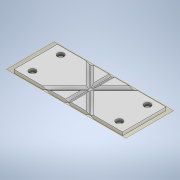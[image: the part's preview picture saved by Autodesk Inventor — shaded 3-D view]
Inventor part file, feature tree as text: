
AUTODESK INVENTOR PART (.ipt)
format: ipt  version: 2020 (Build 240168000, 168)  size: 274,944 bytes
history: native  units: mm
features: chamfer x24, projected_geometry x8, extrude x3, sketch x3, plane x1
ambient origin geometry x8: Origin, YZ Plane, XZ Plane, XY Plane, X Axis, Y Axis, Z Axis, Center Point
bodies: Solid1 (feature_tree)
feature tree (39):
  extrude  "Extrusion1"  Depth=20.0mm
  plane  "Work Plane1"
  extrude  "Extrusion2"  Depth=10.0mm
  chamfer  "Chamfer1"  Distance=10.0mm
  chamfer  "Chamfer2"  Distance=0.5mm
  chamfer  "Chamfer3"  Distance=25.0mm
  chamfer  "Chamfer4"  Distance=0.5mm
  chamfer  "Chamfer5"  Distance=50.0mm
  chamfer  "Chamfer6"  Distance=0.5mm
  chamfer  "Chamfer7"  Distance=50.0mm
  chamfer  "Chamfer8"  Distance=1.5mm
  chamfer  "Chamfer9"  Distance=0.29mm
  chamfer  "Chamfer10"  Distance=0.605mm Angle=60.0deg
  chamfer  "Chamfer11"  Distance=0.605mm Angle=60.0deg
  chamfer  "Chamfer12"  Distance=0.605mm Angle=60.0deg
  chamfer  "Chamfer13"  Distance=0.605mm Angle=60.0deg
  chamfer  "Chamfer14"  Distance=0.605mm Angle=60.0deg
  chamfer  "Chamfer15"  Distance=0.605mm Angle=60.0deg
  chamfer  "Chamfer16"  Distance=0.605mm Angle=60.0deg
  chamfer  "Chamfer17"  Distance=0.605mm Angle=60.0deg
  chamfer  "Chamfer18"  Distance=0.605mm Angle=60.0deg
  chamfer  "Chamfer19"  Distance=0.605mm Angle=60.0deg
  chamfer  "Chamfer20"  Distance=0.605mm Angle=60.0deg
  chamfer  "Chamfer21"  Distance=0.605mm Angle=60.0deg
  chamfer  "Chamfer22"  Distance=0.605mm Angle=60.0deg
  chamfer  "Chamfer23"  Distance=0.605mm Angle=60.0deg
  chamfer  "Chamfer24"  Distance=0.605mm Angle=60.0deg
  extrude  "Extrusion3"  Depth=0.605mm TaperAngle=60.0deg
  sketch  "Sketch1"  dims[d0=50.0mm d1=20.0mm]
  sketch  "Sketch2"  dims[d2=10.0mm d3=10.0mm]
  projected_geometry  "Projected Loop1"
  projected_geometry  "Projected Loop2"
  projected_geometry  "Projected Loop3"
  projected_geometry  "Projected Loop4"
  projected_geometry  "Projected Loop5"
  projected_geometry  "Projected Loop6"
  sketch  "Sketch3"  dims[d4=10.0mm d5=10.0mm d6=0.5mm d7=25.0mm d8=0.5mm d9=50.0mm d10=0.5mm d11=50.0mm d12=1.5mm d13=0.0mm d14=0.29mm d15=0.0mm d16=1.0mm d17=0.605mm d18=60.0deg d19=1.0mm d20=0.605mm d21=60.0deg d22=1.0mm d23=0.605mm d24=60.0deg d25=1.0mm d26=0.605mm d27=60.0deg d28=1.0mm d29=0.605mm d30=60.0deg d31=1.0mm d32=0.605mm d33=60.0deg d34=1.0mm d35=0.605mm d36=60.0deg d37=1.0mm d38=0.605mm d39=60.0deg d40=1.0mm d41=0.605mm d42=60.0deg d43=1.0mm d44=0.605mm d45=60.0deg d46=1.0mm d47=0.605mm d48=60.0deg d49=1.0mm d50=0.605mm d51=60.0deg d52=0.605mm d53=1.0mm d54=60.0deg d55=0.605mm d56=1.0mm d57=60.0deg d58=0.605mm d59=1.0mm d60=60.0deg d61=0.605mm d62=1.0mm d63=60.0deg d64=0.605mm d65=1.0mm d66=60.0deg d67=0.605mm d68=1.0mm d69=60.0deg d70=0.605mm d71=1.0mm d72=60.0deg d73=0.605mm d74=1.0mm d75=60.0deg d76=0.605mm d77=1.0mm d78=60.0deg d79=0.605mm d80=1.0mm d81=60.0deg d82=0.605mm d83=1.0mm d84=60.0deg d85=0.605mm d86=1.0mm d87=60.0deg d88=13.0mm d89=40.0mm d90=3.0mm d91=3.0mm d92=3.0mm d93=3.0mm d94=4.0mm d95=0.0mm]
  projected_geometry  "Projected Loop7"
  projected_geometry  "Projected Loop8"
